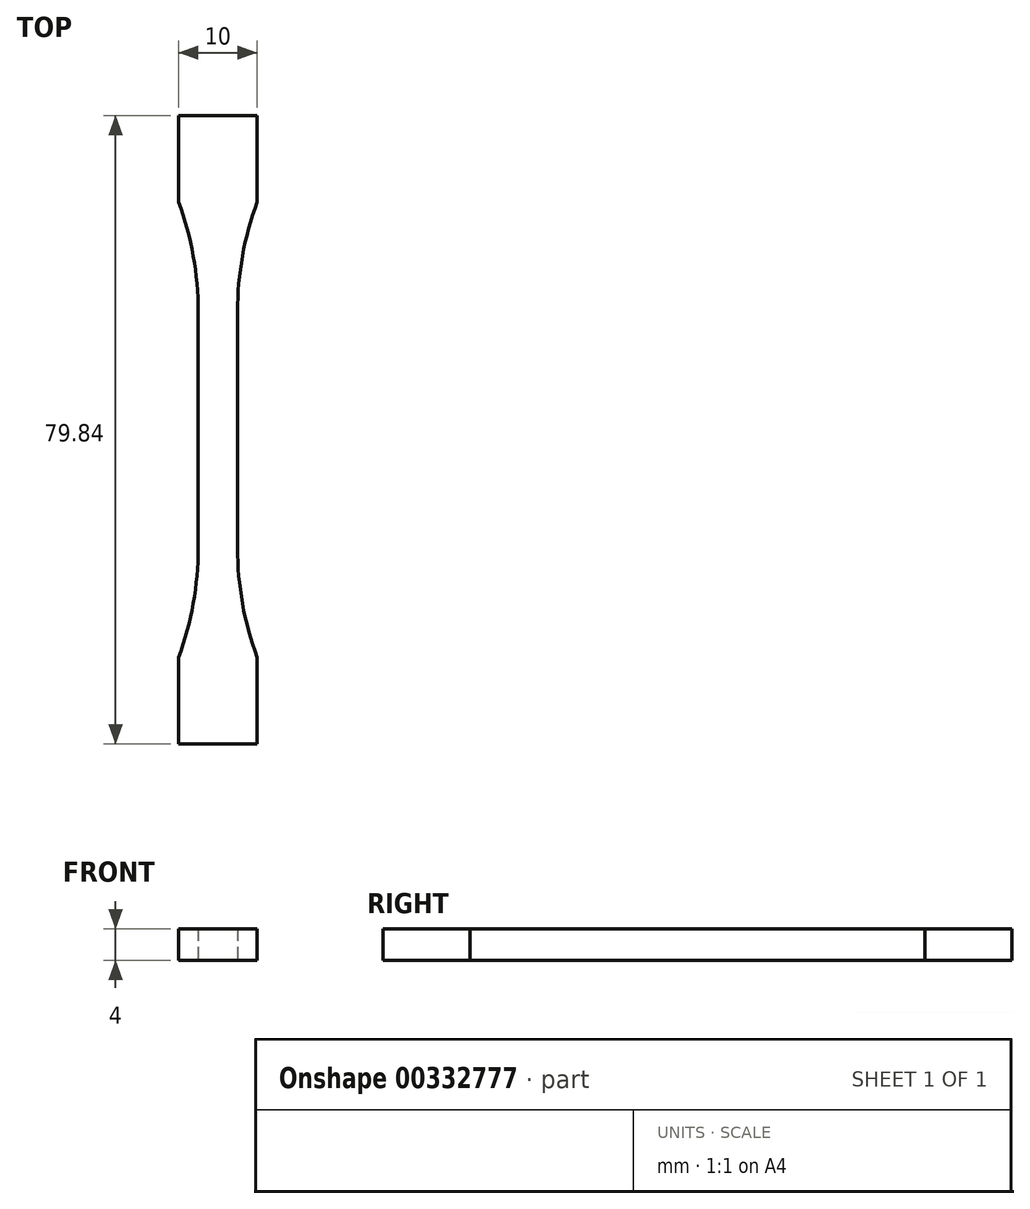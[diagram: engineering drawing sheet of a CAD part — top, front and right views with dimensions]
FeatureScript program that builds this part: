
annotation { "Feature Type Name" : "Feature", "Feature Type Description" : "" }
export const myFeature = defineFeature(function(context is Context, id is Id, definition is map)
    precondition{}
    {
        {
            var Q0;
            Q0=qCreatedBy(makeId("Top.planeOp"),FACE);
            var sketch = newSketch(context, id + "F0", { "sketchPlane" : qUnion([Q0])});
            skLineSegment(sketch, "E0", {"start": v(-2.5, 0) * mm, "end": v(-2.5, 15) * mm});
            skLineSegment(sketch, "E1", {"start": v(-5, 28.92) * mm, "end": v(-5, 39.92) * mm});
            skLineSegment(sketch, "E2", {"start": v(-5, 39.92) * mm, "end": v(0, 39.92) * mm});
            skLineSegment(sketch, "E3", {"start": v(0, 39.92) * mm, "end": v(0, 0) * mm});
            skLineSegment(sketch, "E4", {"start": v(0, 0) * mm, "end": v(-2.5, 0) * mm});
            skArc(sketch, "E5", {"start": v(-2.5, 15) * mm, "mid": v(-3.13, 22.07) * mm, "end": v(-5, 28.92) * mm});
            skSolve(sketch);
        }
        {
            var Q0;
            Q0=makeQuery(id+"F0.imprint","IMPRINT",FACE,{"disambiguationData":[TD([[makeQuery(id+"F0.imprint","IMPRINT",EDGE,{"derivedFrom":sQuery(id+"F0.wireOp",EDGE,"E0")}),-1.0]])]});
            extrude(context, id + "F1", {"entities" : qUnion([Q0]), "depth" : 4 * mm, "offsetDistance" : 25 * mm});
        }
        {
            var Q0;
            Q0=makeQuery(id+"F1.opExtrude","SWEPT_BODY",BODY,{"disambiguationData":[OSD([sQuery(id+"F0.wireOp",EDGE,"E0"),sQuery(id+"F0.wireOp",EDGE,"E1"),sQuery(id+"F0.wireOp",EDGE,"E2"),sQuery(id+"F0.wireOp",EDGE,"E3"),sQuery(id+"F0.wireOp",EDGE,"E4"),sQuery(id+"F0.wireOp",EDGE,"E5")])]});
            var Q1;
            Q1=makeQuery(id+"F1.opExtrude","SWEPT_FACE",FACE,{"disambiguationData":[OSD([sQuery(id+"F0.wireOp",EDGE,"E3")])]});
            mirror(context, id + "F2", {"operationType" : NewBodyOperationType.ADD, "entities" : qUnion([Q0]), "mirrorPlane" : qUnion([Q1])});
        }
        {
            var Q0;
            Q0=makeQuery(id+"F1.opExtrude","SWEPT_BODY",BODY,{"disambiguationData":[OSD([sQuery(id+"F0.wireOp",EDGE,"E0"),sQuery(id+"F0.wireOp",EDGE,"E1"),sQuery(id+"F0.wireOp",EDGE,"E2"),sQuery(id+"F0.wireOp",EDGE,"E3"),sQuery(id+"F0.wireOp",EDGE,"E4"),sQuery(id+"F0.wireOp",EDGE,"E5")])]});
            var Q1;
            {var subQ0=makeQuery(id+"F1.opExtrude","SWEPT_FACE",FACE,{"disambiguationData":[OSD([sQuery(id+"F0.wireOp",EDGE,"E4")])]});Q1=makeQuery(id+"F2.boolean.opBoolean","MERGE",FACE,{"derivedFrom":[subQ0,makeQuery(id+"F2.opPattern","COPY",FACE,{"derivedFrom":subQ0,"instanceName":"1"})]});}
            mirror(context, id + "F3", {"operationType" : NewBodyOperationType.ADD, "entities" : qUnion([Q0]), "mirrorPlane" : qUnion([Q1])});
        }
    });
